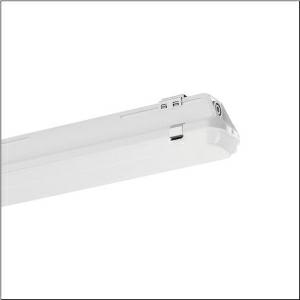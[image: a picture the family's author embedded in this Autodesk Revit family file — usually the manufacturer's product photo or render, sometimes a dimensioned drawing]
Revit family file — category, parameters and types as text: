
# Revit family: monsun_r__11_51fp12mp480h_cfdd
name_source: partatom
category: Lighting Fixtures
units: mm (PartAtom-declared; Revit-internal decimal feet)

## family parameters
Cut with Voids When Loaded = No
Host = Face
Light Source = No
Part Type = Normal
Room Calculation Point = No
Round Connector Dimension = Use Diameter
Shared = No

## types (1)
- --- (1 x LED, 7990 lm, 45.4 W, 4000K)
    Apparent Load = 45 VA
    CIE Flux Codes = 65 88 97 97 100
    Color Rendering = 80
    Color Temperature = 4000K
    Default Elevation = 1800 mm
    Description = Monsun® 11, damp-proof luminaire, chain hanger, primary light control with lens, primary optical cover: enclosure, of PMMA, light emission: direct distribution, primary light characteristic: symmetric, installation type: suspended mounting, surface-mounted, horizontal mounting, vertical mounting, LED, rated luminous flux: 7.990lm, luminous efficacy: 176lm/W, light colour: 840, colour temperature: 4000K, control gear: ON/OFF Multilumen, with terminal, 3-pole, max. 2.5mm², mains connection: 220..240V, AC, 50/60Hz, rated input power: 45W, luminaire housing, of glass-fibre reinforced polyester, uncoated, bright grey, incl. chain hanger, length: 1.590mm, width: 90mm, height: 88mm, clip for enclosure, of stainless steel (V2A), ceiling mounting element, of stainless steel (V2A), chain hanger, of stainless steel (V2A), protection rating (complete): IP66, insulation class (complete): insulation class I (protective earthing), certification: CE, ENEC, VDE, UKCA, protection symbol: D, impact resistance: IK04, permissible operating ambient temperature: -35..+40°C, standard: EN 50419, EN 60598-2-1, no direct snow, no direct sun, no direct rain, for indoor or canopied outdoor use, corresponds to IFS (International Featured Standards) requirements for safety and quality in the food industry, contact your sales advisor before using the luminaires in applications with unclear chemical exposure, large temperature fluctuations or condensation-forming humidity, LABS conformity tested according to VDMA 24364:2018-05, packaging unit: 1 piece
    Height = 89 mm
    Lamp = 1 x LED
    Lamp Light Flux = 7990 lm
    Lamp Power = 45.4 W
    Lamp count = 1
    Length = 1590 mm
    Luminous efficacy = 176 lm/W
    Manufacturer = Siteco
    ModVariant = No
    Model = 51FP12MP480H
    Mounting Place = Ceiling
    Mounting Type = Surface mounted
    Number of Poles = 1
    OnlyDefault = Yes
    Power Factor = 1
    Product Name = Monsun® 11
    Product group = damp-proof luminaire
    ProductGroupID = 301
    Protection Class = Protection class I
    Protection Degree = IP 66
    RLX_Detail_Level = 1
    RLX_Emergency_Light_Flux = 0 lm
    RLX_Emergency_Type = 0
    RLX_Emergency_Type_DB = No
    RlxData = <blob elided: 89993 chars, md5=fdaf42c2>
    Socket = socket
    Standby Power = 0 W
    System Light Flux = 7990 lm
    System Power = 45 W
    Type Comments = factory setting: luminous flux: 100 % | (A | C | E) | 105 mA
    Type Image = l_1349237.jpg
    URL = http://relux.com
    VarID = @adj_219747
    Voltage = 0 V
    Weight = 0.00 kg
    Width = 90 mm

## geometry (parser evidence)
native form markers: Blend x4, Sweep x9
no freeform markers — native parametric forms only
